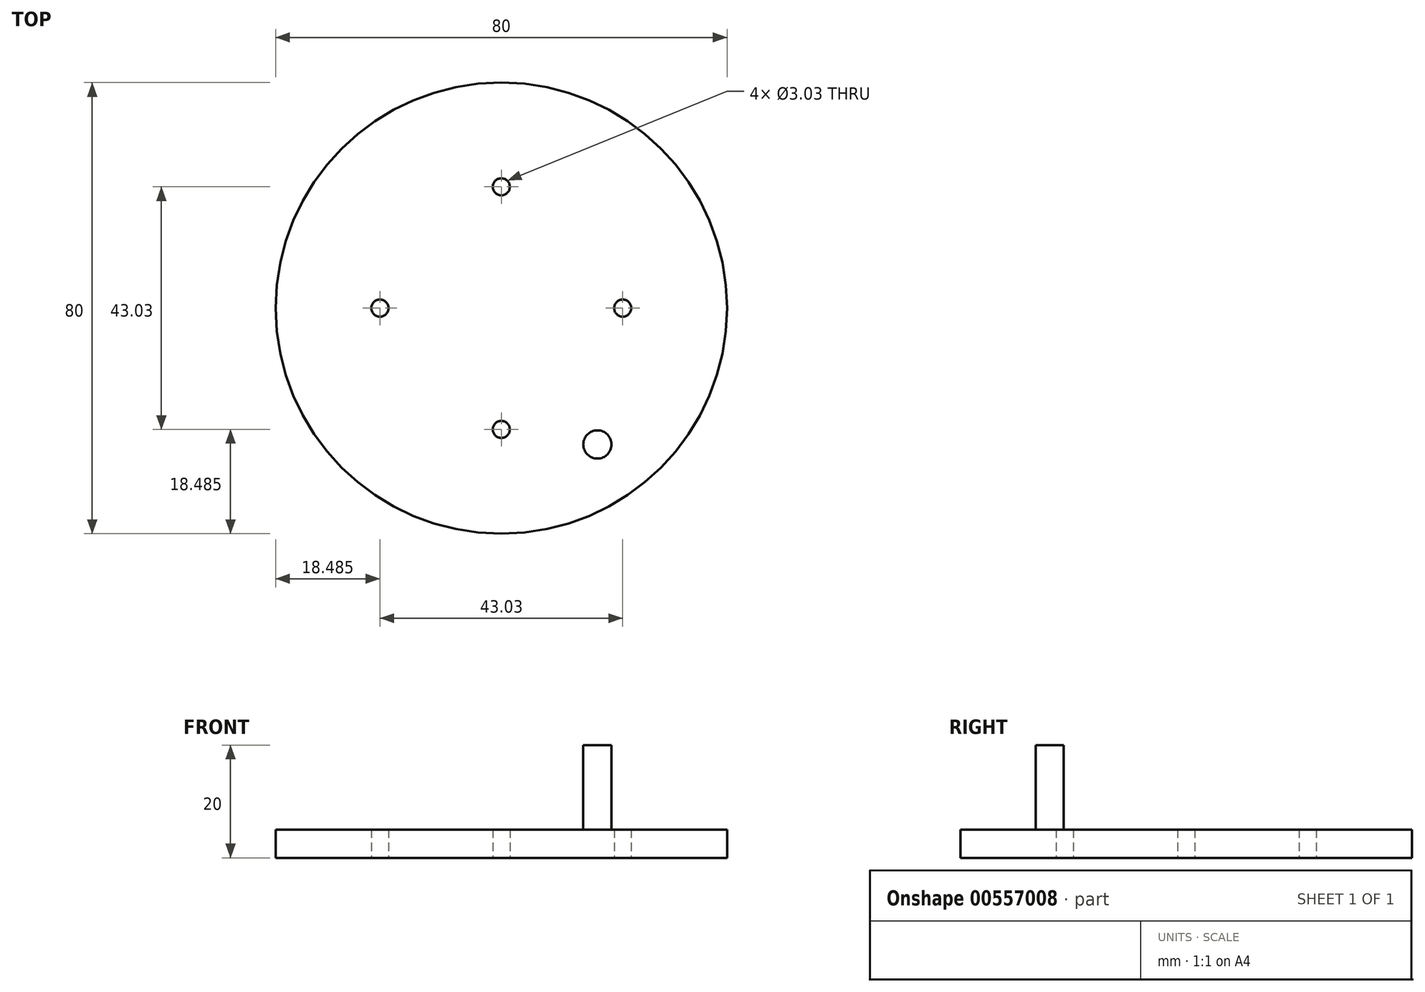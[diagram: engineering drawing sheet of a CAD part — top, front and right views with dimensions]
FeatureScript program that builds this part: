
annotation { "Feature Type Name" : "Feature", "Feature Type Description" : "" }
export const myFeature = defineFeature(function(context is Context, id is Id, definition is map)
    precondition{}
    {
        {
            var Q0;
            Q0=qCreatedBy(makeId("Top.planeOp"),FACE);
            var sketch = newSketch(context, id + "F0", { "sketchPlane" : qUnion([Q0])});
            skCircle(sketch, "E0", {"center": v(0, 0) * mm, "radius": 40 * mm});
            skCircle(sketch, "E1", {"center": v(0, 21.52) * mm, "radius": 1.51 * mm});
            skCircle(sketch, "E2", {"center": v(-21.52, 0) * mm, "radius": 1.51 * mm});
            skCircle(sketch, "E3", {"center": v(21.52, 0) * mm, "radius": 1.51 * mm});
            skCircle(sketch, "E4", {"center": v(0, -21.52) * mm, "radius": 1.51 * mm});
            skCircle(sketch, "E5", {"center": v(17.03, -24.18) * mm, "radius": 2.5 * mm});
            skSolve(sketch);
        }
        {
            var Q0;
            Q0=qSketchRegion(id+"F0",true);
            extrude(context, id + "F1", {"entities" : qUnion([Q0]), "depth" : 5 * mm});
        }
        {
            var Q0;
            Q0=makeQuery(id+"F0.imprint","IMPRINT",FACE,{"disambiguationData":[TD([[makeQuery(id+"F0.imprint","IMPRINT",EDGE,{"derivedFrom":sQuery(id+"F0.wireOp",EDGE,"E5")}),1.0]])]});
            extrude(context, id + "F2", {"entities" : qUnion([Q0]), "operationType" : NewBodyOperationType.ADD, "depth" : 20 * mm, "offsetDistance" : 25 * mm});
        }
    });
